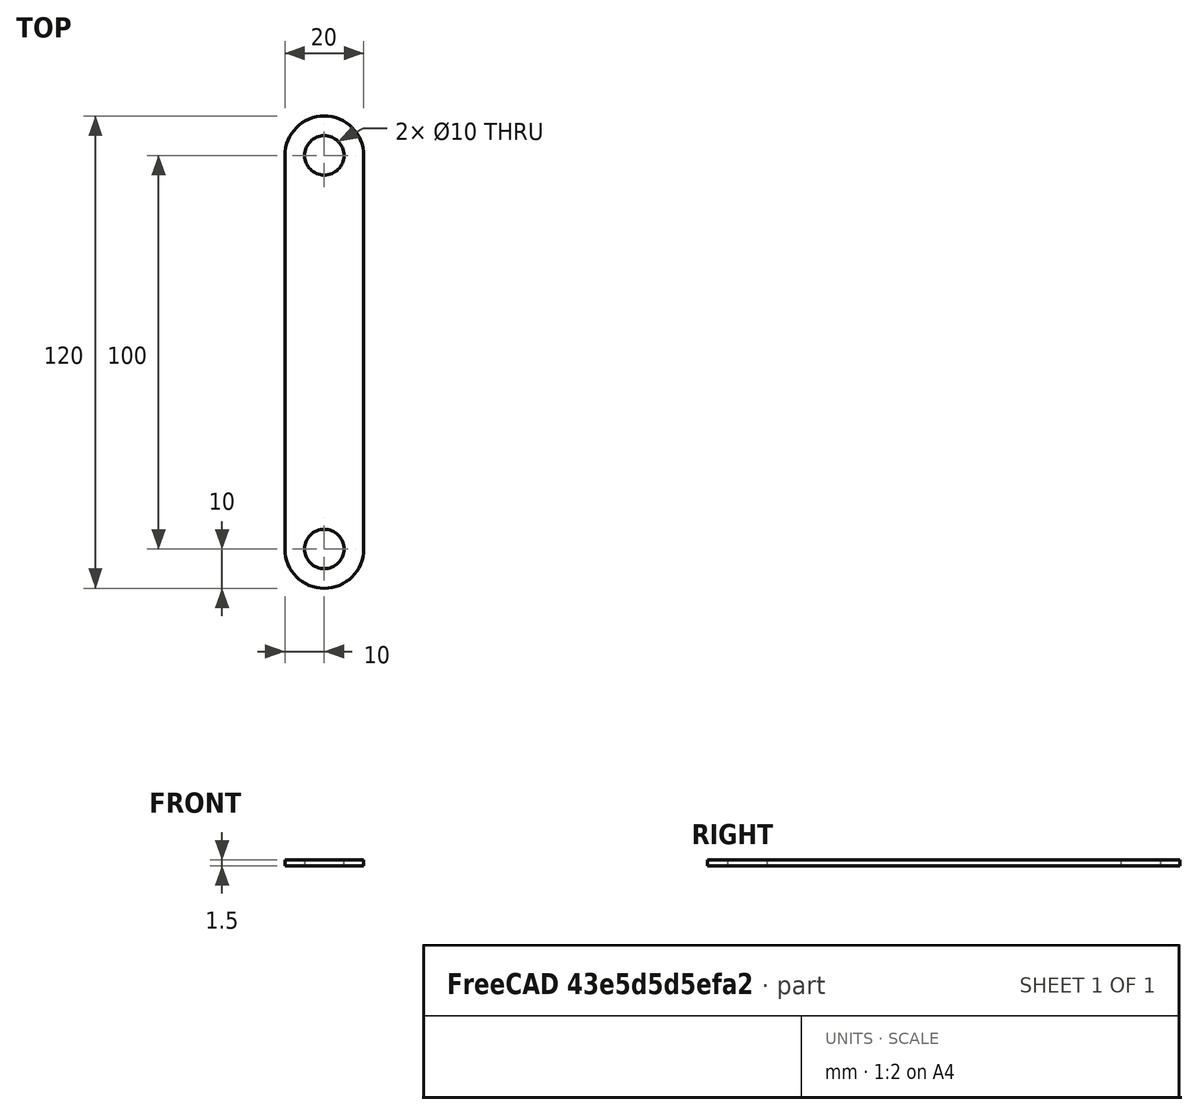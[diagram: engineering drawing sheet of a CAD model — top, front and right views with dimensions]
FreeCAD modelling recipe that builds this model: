
FCSTD DOCUMENT  (FreeCAD 0.21R33694 (Git))
Label: Leg_frame_pitch
License: All rights reserved
LicenseURL: https://en.wikipedia.org/wiki/All_rights_reserved
objects: Sketcher::SketchObject×1, PartDesign::Pad×1, PartDesign::Body×1
note: 4 computed .brp shape members not serialized (recipe doc carries the construction recipe); baked Part::Feature solids carry a one-line shape summary decoded from their .brp

FEATURE [Sketcher::SketchObject] Sketch
  FullyConstrained = true
  MapMode = 5
  Support = -> [XY_Plane]
  sketch-geometry (7):
    g0: Circle CenterX=0 CenterY=0 CenterZ=0 NormalX=0 NormalY=0 NormalZ=1 AngleXU=0 Radius=5
    g1: ArcOfCircle CenterX=0 CenterY=0 CenterZ=0 NormalX=0 NormalY=0 NormalZ=1 AngleXU=0 Radius=10 StartAngle=3.14159 EndAngle=6.28319
    g2: LineSegment StartX=0 StartY=0 StartZ=0 EndX=0 EndY=100 EndZ=0
    g3: ArcOfCircle CenterX=0 CenterY=100 CenterZ=0 NormalX=0 NormalY=0 NormalZ=1 AngleXU=0 Radius=10 StartAngle=4e-16 EndAngle=3.14159
    g4: LineSegment StartX=-10 StartY=-3.2e-15 StartZ=0 EndX=-10 EndY=100 EndZ=0
    g5: LineSegment StartX=10 StartY=-2.4e-15 StartZ=0 EndX=10 EndY=100 EndZ=0
    g6: Circle CenterX=0 CenterY=100 CenterZ=0 NormalX=0 NormalY=0 NormalZ=1 AngleXU=0 Radius=5
  constraints (15):
    c: Coincident(g0,g-1)
    c: Coincident(g1,g0)
    c: Coincident(g2,g0)
    c: PointOnObject(g2,g-2)
    c: DistanceY(g2,g2) = 100
    c: Coincident(g3,g2)
    c: Tangent(g3,g4) = 1.5708
    c: Tangent(g1,g4) = 1.5708
    c: Tangent(g1,g5) = -1.5708
    c: Tangent(g3,g5) = -1.5708
    c: Equal(g3,g1)
    c: Diameter(g1) = 20
    c: Diameter(g0) = 10
    c: Coincident(g6,g3)
    c: Equal(g6,g0)
FEATURE [PartDesign::Pad] Pad
  Direction = (0,0,1)
  Length = 1.5
  Length2 = 10
  Profile = -> Sketch
  ReferenceAxis = -> Sketch [N_Axis]
  Type = 0
FEATURE [PartDesign::Body] Body
  Group = -> [Sketch,Pad]
  Origin = -> Origin
  Tip = -> Pad
